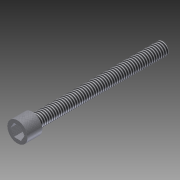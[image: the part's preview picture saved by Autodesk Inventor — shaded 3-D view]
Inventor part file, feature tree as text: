
AUTODESK INVENTOR PART (.ipt)
format: ipt  version: 2012 (Build 160160000, 160)  size: 93,184 bytes
history: native  units: in
note: dims shown in document units (in); Inventor stores cm internally (conversion verified against a paired STEP export)
features: extrude x2, sketch x1, thread x1
ambient origin geometry x8: Origin, YZ Plane, XZ Plane, XY Plane, X Axis, Y Axis, Z Axis, Center Point
bodies: Solid1 (feature_tree)
feature tree (4):
  sketch  "Sketch1"  dims[d0=0.164in d1=0.27in d2=1.75in d3=0.0in d4=0.2in d5=0.0in d6=1.0in d7=0.0in]
  extrude  "Extrusion1"  Depth=0.27in
  extrude  "Extrusion2"  Depth=1.75in TaperAngle=0.0deg
  thread  "Thread1"  [1 undecoded]
note: 1 required parameter value undecoded (feature->parameter linkage not recoverable at this tier; creation-order binding heuristic only, values carry confidence <= 0.55)
